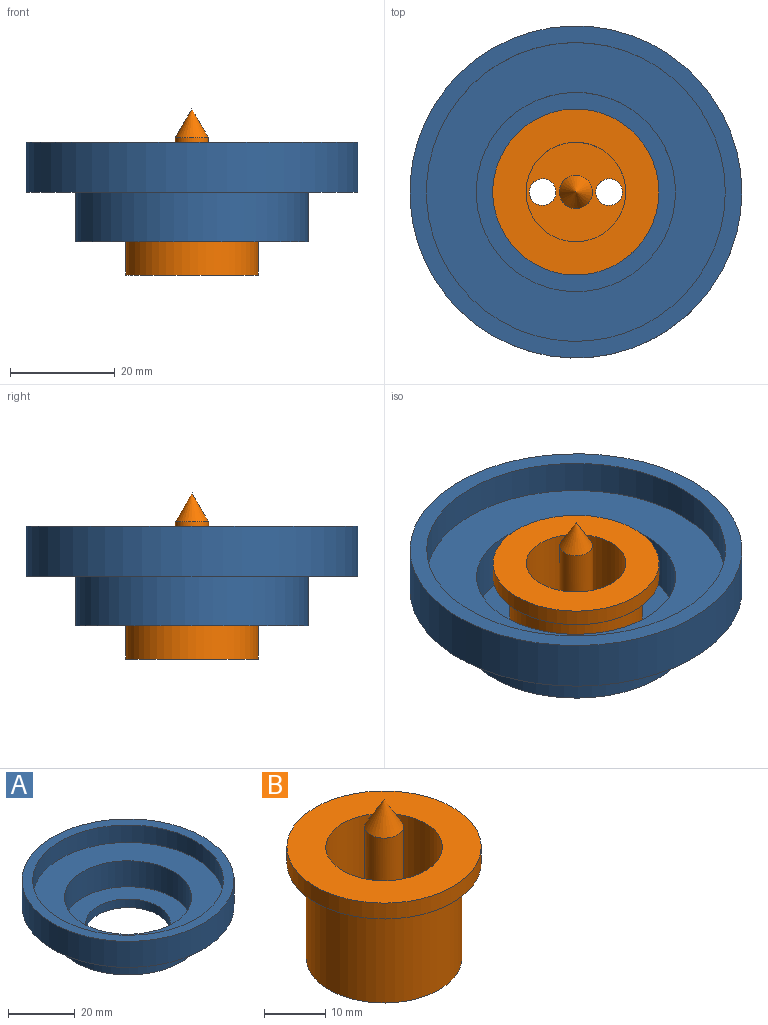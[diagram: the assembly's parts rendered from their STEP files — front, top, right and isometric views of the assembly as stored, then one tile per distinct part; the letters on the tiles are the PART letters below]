
ASSEMBLY  parts=2 mates=1
PART A: 10 faces, bbox 63.5x63.5x19.1 mm
  f0: plane 63.5x63.5mm, normal (0,0,-1), area 1615.1mm2, adj f1,f9
  f1: cylinder r=22.23mm len=44.45mm, axis (0,0,1), area 1330.1mm2, adj f0,f2
  f2: plane 44.45x44.45mm, normal (0,0,-1), area 1045.1mm2, adj f1,f3
  f3: cylinder r=12.7mm len=25.4mm, axis (0,0,1), area 253.4mm2, adj f2,f4
  f4: plane 38.1x38.1mm, normal (0,0,1), area 633.4mm2, adj f3,f5
  f5: cylinder r=19.05mm len=38.1mm, axis (0,0,1), area 1140.1mm2, adj f4,f6
  f6: plane 57.15x57.15mm, normal (0,0,1), area 1425.1mm2, adj f5,f7
  f7: cylinder r=28.57mm len=57.15mm, axis (0,0,1), area 1140.1mm2, adj f6,f8
  f8: plane 63.5x63.5mm, normal (0,0,1), area 601.7mm2, adj f7,f9
  f9: cylinder r=31.75mm len=63.5mm, axis (0,0,1), area 1900.2mm2, adj f0,f8
PART B: 11 faces, bbox 31.8x31.8x31.8 mm
  f0: plane 25.4x25.4mm, normal (0,0,-1), area 465.8mm2, adj f8,f9,f10
  f1: cone r=3.17mm half-angle=30deg, axis (0,0,-1), area 63.3mm2, adj f2
  f2: cylinder r=3.17mm len=19.9mm, axis (0,0,1), area 397mm2, adj f1,f3
  f3: plane 19.05x19.05mm, normal (0,0,1), area 212.4mm2, adj f2,f4,f9,f10
  f4: cylinder r=9.53mm len=19.05mm, axis (0,0,1), area 950.1mm2, adj f3,f5
  f5: plane 31.75x31.75mm, normal (0,0,1), area 506.7mm2, adj f4,f6
  f6: cylinder r=15.88mm len=31.75mm, axis (0,0,1), area 316.7mm2, adj f5,f7
  f7: plane 31.75x31.75mm, normal (0,0,-1), area 285mm2, adj f6,f8
  f8: cylinder r=12.7mm len=25.4mm, axis (0,0,1), area 1520.1mm2, adj f0,f7
  f9: cylinder r=2.55mm len=6.35mm, axis (0,0,-1), area 101.8mm2, adj f0,f3
  f10: cylinder r=2.55mm len=6.35mm, axis (0,0,-1), area 101.8mm2, adj f0,f3
PLACE A t=(0,0,6.35)mm
PLACE B at identity
MATE slider A.f1 <-> B.f1  axis (0,0,1) through (0,0,9.52)mm
